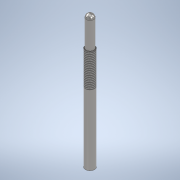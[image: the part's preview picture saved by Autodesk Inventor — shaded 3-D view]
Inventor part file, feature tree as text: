
AUTODESK INVENTOR PART (.ipt)
format: ipt  version: 2020 (Build 240168000, 168)  size: 105,984 bytes
history: native  units: mm
features: extrude x2, sketch x2, thread x1, fillet x1
ambient origin geometry x8: Origin, YZ Plane, XZ Plane, XY Plane, X Axis, Y Axis, Z Axis, Center Point
bodies: Solid1 (feature_tree)
feature tree (6):
  extrude  "Extrusion1"  Depth=34.0mm TaperAngle=0.0deg
  extrude  "Extrusion2"  Depth=10.0mm TaperAngle=0.0deg
  thread  "Thread1"  [1 undecoded]
  fillet  "Fillet1"  Radius=1.25mm
  sketch  "Sketch1"  dims[d0=3.0mm d1=34.0mm d2=0.0mm]
  sketch  "Sketch2"  dims[d3=2.5mm d4=10.0mm d5=0.0mm d6=11.0mm d7=23.0mm d8=1.25mm]
note: 1 required parameter value undecoded (feature->parameter linkage not recoverable at this tier; creation-order binding heuristic only, values carry confidence <= 0.55)
